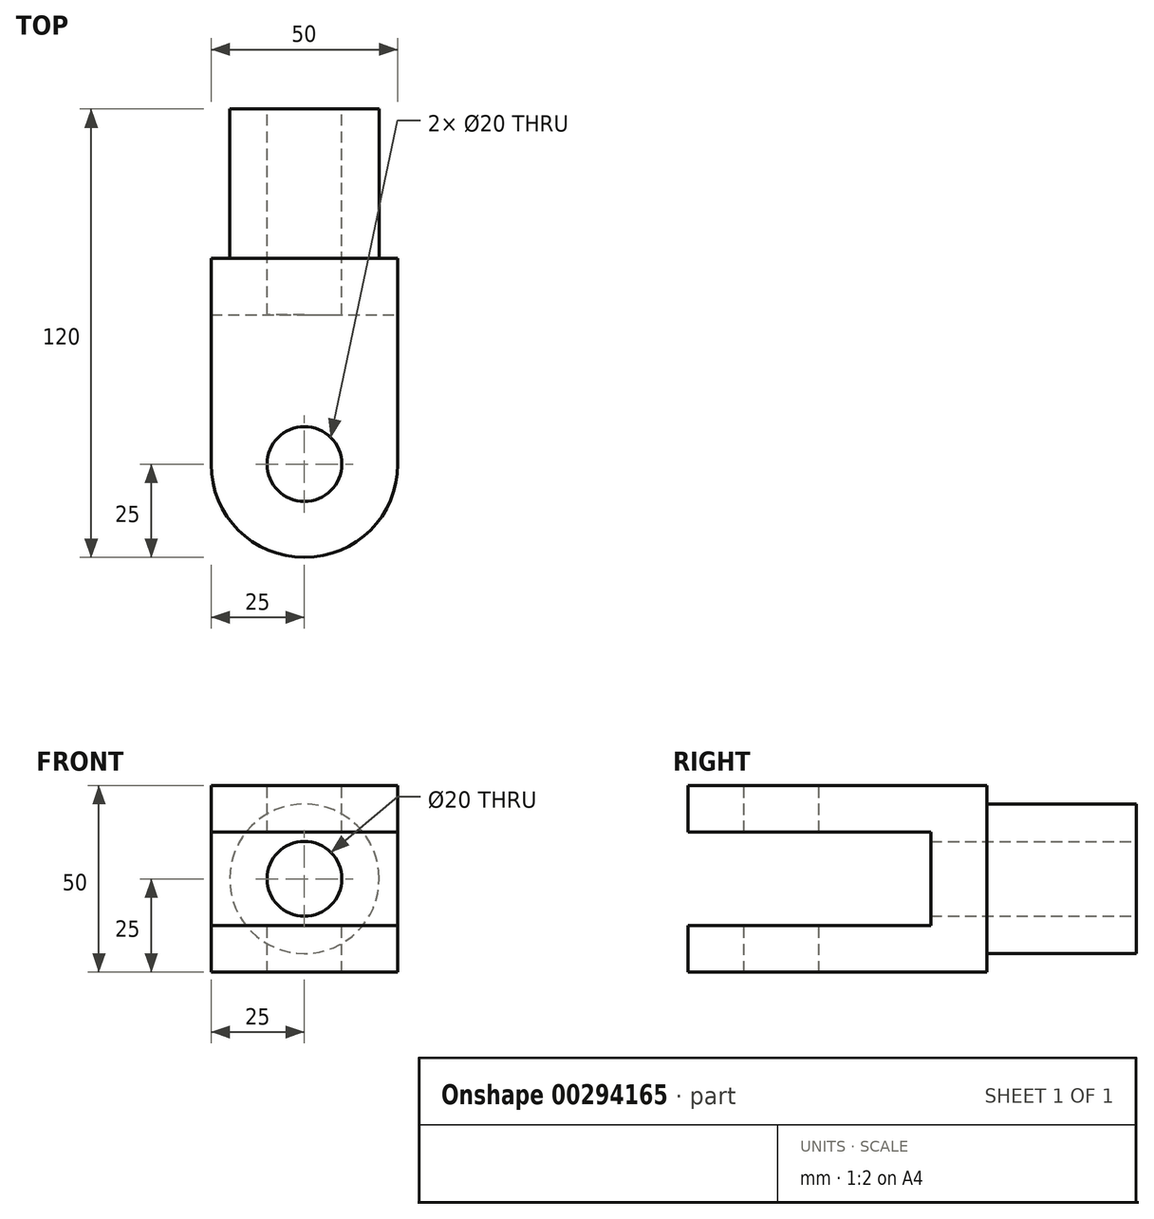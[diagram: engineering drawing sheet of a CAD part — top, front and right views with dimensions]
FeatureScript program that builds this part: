
annotation { "Feature Type Name" : "Feature", "Feature Type Description" : "" }
export const myFeature = defineFeature(function(context is Context, id is Id, definition is map)
    precondition{}
    {
        {
            var Q0;
            Q0=qCreatedBy(makeId("Front.planeOp"),FACE);
            var sketch = newSketch(context, id + "F0", { "sketchPlane" : qUnion([Q0])});
            skLineSegment(sketch, "E0.bottom", {"start": v(25, -25) * mm, "end": v(-25, -25) * mm});
            skLineSegment(sketch, "E0.top", {"start": v(25, 25) * mm, "end": v(-25, 25) * mm});
            skLineSegment(sketch, "E0.left", {"start": v(25, -25) * mm, "end": v(25, 25) * mm});
            skLineSegment(sketch, "E0.right", {"start": v(-25, -25) * mm, "end": v(-25, 25) * mm});
            skPoint(sketch, "E0.middle", {"position": v(0, 0) * mm});
            skSolve(sketch);
        }
        {
            var Q0;
            Q0 = qSketchRegion(id + "F0", true);
            extrude(context, id + "F1", {"entities" : qUnion([Q0]), "endBound" : BoundingType.SYMMETRIC, "depth" : 15 * mm});
        }
        {
            var Q0;
            Q0=makeQuery(id+"F1.opExtrude","CAP_FACE",FACE,{"disambiguationData":[OSD([sQuery(id+"F0.wireOp",EDGE,"E0.bottom"),sQuery(id+"F0.wireOp",EDGE,"E0.top"),sQuery(id+"F0.wireOp",EDGE,"E0.left"),sQuery(id+"F0.wireOp",EDGE,"E0.right")])],"isStart":false});
            var sketch = newSketch(context, id + "F2", { "sketchPlane" : qUnion([Q0])});
            skLineSegment(sketch, "E1.bottom", {"start": v(25, -25) * mm, "end": v(-25, -25) * mm});
            skLineSegment(sketch, "E1.top", {"start": v(25, -12.5) * mm, "end": v(-25, -12.5) * mm});
            skLineSegment(sketch, "E1.left", {"start": v(25, -25) * mm, "end": v(25, -12.5) * mm});
            skLineSegment(sketch, "E1.right", {"start": v(-25, -25) * mm, "end": v(-25, -12.5) * mm});
            skLineSegment(sketch, "E2.bottom", {"start": v(-25, 25) * mm, "end": v(25, 25) * mm});
            skLineSegment(sketch, "E2.top", {"start": v(-25, 12.5) * mm, "end": v(25, 12.5) * mm});
            skLineSegment(sketch, "E2.left", {"start": v(-25, 25) * mm, "end": v(-25, 12.5) * mm});
            skLineSegment(sketch, "E2.right", {"start": v(25, 25) * mm, "end": v(25, 12.5) * mm});
            skSolve(sketch);
        }
        {
            var Q0;
            Q0 = qSketchRegion(id + "F2", true);
            extrude(context, id + "F3", {"entities" : qUnion([Q0]), "operationType" : NewBodyOperationType.ADD, "depth" : 65 * mm});
        }
        {
            var Q0;
            Q0=makeQuery(id+"F3.boolean.opBoolean","MERGE",FACE,{"derivedFrom":[makeQuery(id+"F1.opExtrude","SWEPT_FACE",FACE,{"disambiguationData":[OSD([sQuery(id+"F0.wireOp",EDGE,"E0.top")])]}),makeQuery(id+"F3.opExtrude","SWEPT_FACE",FACE,{"disambiguationData":[OSD([sQuery(id+"F2.wireOp",EDGE,"E2.bottom")])]})]});
            var sketch = newSketch(context, id + "F4", { "sketchPlane" : qUnion([Q0])});
            skCircle(sketch, "E3", {"center": v(0, -47.5) * mm, "radius": 10 * mm});
            skSolve(sketch);
        }
        {
            var Q0;
            Q0=sQuery(id+"F4.wireOp",VERTEX,"E3.center");
            var Q1;
            Q1=makeQuery(id+"F1.opExtrude","SWEPT_BODY",BODY,{"disambiguationData":[OSD([sQuery(id+"F0.wireOp",EDGE,"E0.bottom"),sQuery(id+"F0.wireOp",EDGE,"E0.top"),sQuery(id+"F0.wireOp",EDGE,"E0.left"),sQuery(id+"F0.wireOp",EDGE,"E0.right")])]});
            hole(context, id + "F5", {"style" : HoleStyle.SIMPLE, "endStyle" : HoleEndStyle.THROUGH, "holeDiameter" : 20 * mm, "tappedDepth" : 12 * mm, "tapClearance" : 3, "locations" : qUnion([Q0]), "scope" : qUnion([Q1])});
        }
        {
            var Q0;
            Q0=makeQuery(id+"F3.opExtrude","CAP_EDGE",EDGE,{"disambiguationData":[OSD([sQuery(id+"F2.wireOp",EDGE,"E1.right")])],"isStart":false});
            fillet(context, id + "F6", {"entities" : qUnion([Q0]), "radius" : 25 * mm, "tangentPropagation" : true, "allowEdgeOverflow" : false});
        }
        {
            var Q0;
            Q0=makeQuery(id+"F3.opExtrude","CAP_EDGE",EDGE,{"disambiguationData":[OSD([sQuery(id+"F2.wireOp",EDGE,"E2.right")])],"isStart":false});
            var Q1;
            Q1=makeQuery(id+"F3.opExtrude","CAP_EDGE",EDGE,{"disambiguationData":[OSD([sQuery(id+"F2.wireOp",EDGE,"E1.left")])],"isStart":false});
            var Q2;
            Q2=makeQuery(id+"F3.opExtrude","CAP_EDGE",EDGE,{"disambiguationData":[OSD([sQuery(id+"F2.wireOp",EDGE,"E2.left")])],"isStart":false});
            fillet(context, id + "F7", {"entities" : qUnion([Q0, Q1, Q2]), "radius" : 25 * mm, "tangentPropagation" : true, "allowEdgeOverflow" : false});
        }
        {
            var Q0;
            Q0=makeQuery(id+"F1.opExtrude","CAP_FACE",FACE,{"disambiguationData":[OSD([sQuery(id+"F0.wireOp",EDGE,"E0.bottom"),sQuery(id+"F0.wireOp",EDGE,"E0.top"),sQuery(id+"F0.wireOp",EDGE,"E0.left"),sQuery(id+"F0.wireOp",EDGE,"E0.right")])],"isStart":true});
            var sketch = newSketch(context, id + "F8", { "sketchPlane" : qUnion([Q0])});
            skCircle(sketch, "E4", {"center": v(0, 0) * mm, "radius": 20 * mm});
            skSolve(sketch);
        }
        {
            var Q0;
            Q0 = qSketchRegion(id + "F8", true);
            extrude(context, id + "F9", {"entities" : qUnion([Q0]), "operationType" : NewBodyOperationType.ADD, "depth" : 40 * mm});
        }
        {
            var Q0;
            Q0=makeQuery(id+"F9.opExtrude","CAP_FACE",FACE,{"disambiguationData":[OSD([sQuery(id+"F8.wireOp",EDGE,"E4")])],"isStart":false});
            var sketch = newSketch(context, id + "F10", { "sketchPlane" : qUnion([Q0])});
            skCircle(sketch, "E5", {"center": v(0, 0) * mm, "radius": 20 * mm});
            skSolve(sketch);
        }
        {
            var Q0;
            Q0=sQuery(id+"F10.wireOp",VERTEX,"E5.center");
            var Q1;
            Q1=makeQuery(id+"F1.opExtrude","SWEPT_BODY",BODY,{"disambiguationData":[OSD([sQuery(id+"F0.wireOp",EDGE,"E0.bottom"),sQuery(id+"F0.wireOp",EDGE,"E0.top"),sQuery(id+"F0.wireOp",EDGE,"E0.left"),sQuery(id+"F0.wireOp",EDGE,"E0.right")])]});
            hole(context, id + "F11", {"style" : HoleStyle.SIMPLE, "endStyle" : HoleEndStyle.THROUGH, "holeDiameter" : 20 * mm, "tappedDepth" : 12 * mm, "tapClearance" : 3, "locations" : qUnion([Q0]), "scope" : qUnion([Q1])});
        }
    });
